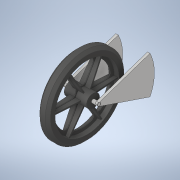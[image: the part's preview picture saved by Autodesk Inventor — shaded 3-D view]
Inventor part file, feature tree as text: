
AUTODESK INVENTOR PART (.ipt)
format: ipt  version: 2021 (Build 250183000, 183)  size: 360,960 bytes
history: native  units: mm
features: other x3, extrude x3, sketch x3, thicken_offset x2, plane x1, mirror x1
ambient origin geometry x8: Origin, YZ Plane, XZ Plane, XY Plane, X Axis, Y Axis, Z Axis, Center Point
bodies: Solid1 (feature_tree)
feature tree (13):
  other  "wheel.ipt"
  extrude  "Extrusion1"  TaperAngle=0.0deg  [1 undecoded]
  extrude  "Extrusion2"  TaperAngle=0.0deg  [1 undecoded]
  extrude  "Extrusion3"  Depth=30.0mm
  plane  "Work Plane1"
  mirror  "Mirror1"
  thicken_offset  "Thicken1"
  thicken_offset  "Thicken2"
  other  "Solid19::wheel.ipt"
  other  "TaggingFeature1"
  sketch  "Sketch1"  dims[d0=5.0mm d2=0.0mm]
  sketch  "Sketch2"  dims[d4=0.0mm d6=0.0mm]
  sketch  "Sketch3"  dims[d9=30.0mm d11=30.0mm]
note: 2 required parameter values undecoded (feature->parameter linkage not recoverable at this tier; creation-order binding heuristic only, values carry confidence <= 0.55)
